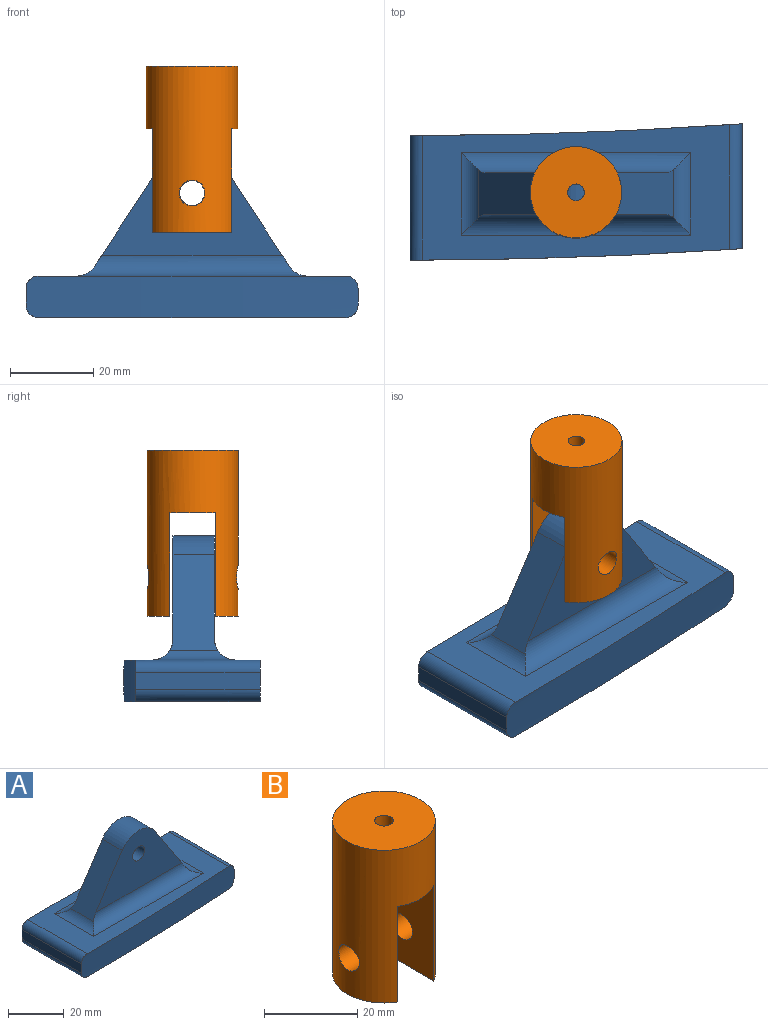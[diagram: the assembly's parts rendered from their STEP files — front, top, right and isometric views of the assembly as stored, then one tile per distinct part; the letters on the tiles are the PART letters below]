
ASSEMBLY  parts=2 mates=1
PART A: 20 faces, bbox 80x32.8x40 mm
  f0: plane 43.47x25mm, normal (0,1,0), area 641.4mm2, adj f8,f9,f10,f11,f12
  f1: plane 43.47x25mm, normal (0,-1,0), area 641.4mm2, adj f8,f9,f10,f11,f15
  f2: plane 74x32.63mm, normal (0,0,1), area 1113.5mm2, adj f4,f6,f12,f13,f14,f15,f18,f19
  f3: plane 30x4mm, normal (-1,0,0), area 120mm2, adj f4,f6,f17,f19
  f4: cylinder r=1158mm len=80mm, axis (0,0,-1), area 792.9mm2, adj f2,f3,f5,f7,f16,f17,f18,f19
  f5: plane 30.07x4mm, normal (1,0,0), area 120.3mm2, adj f4,f6,f16,f18
  f6: cylinder r=1128mm len=80mm, axis (0,0,-1), area 792.9mm2, adj f2,f3,f5,f7,f16,f17,f18,f19
  f7: plane 74x32.63mm, normal (0,0,-1), area 2221.8mm2, adj f4,f6,f16,f17
  f8: cylinder r=3mm len=10mm, axis (0,-1,0), area 188.5mm2, adj f0,f1
  f9: cylinder r=10mm len=16.75mm, axis (0,-1,0), area 198.5mm2, adj f0,f1,f10,f11
  f10: plane 23.2x15.15mm, normal (0.84,0,0.55), area 278.8mm2, adj f0,f1,f9,f12,f14,f15
  f11: plane 23.2x15.15mm, normal (-0.84,0,0.55), area 278.8mm2, adj f0,f1,f9,f12,f13,f15
  f12: cylinder r=5mm len=55.41mm, axis (-1,0,0), area 383.3mm2, adj f0,f2,f10,f11,f13,f14
  f13: cylinder r=5mm len=20mm, axis (0,-1,0), area 76.6mm2, adj f2,f11,f12,f15
  f14: cylinder r=5mm len=20mm, axis (0,-1,0), area 76.6mm2, adj f2,f10,f12,f15
  f15: cylinder r=5mm len=55.41mm, axis (1,0,0), area 383.3mm2, adj f1,f2,f10,f11,f13,f14
  f16: cylinder r=3mm len=30.28mm, axis (0,1,0), area 141.7mm2, adj f4,f5,f6,f7
  f17: cylinder r=3mm len=30mm, axis (0,-1,0), area 141.4mm2, adj f3,f4,f6,f7
  f18: cylinder r=3mm len=30.28mm, axis (0,-1,0), area 141.7mm2, adj f2,f4,f5,f6
  f19: cylinder r=3mm len=30mm, axis (0,1,0), area 141.4mm2, adj f2,f3,f4,f6
PART B: 11 faces, bbox 22x22x40 mm
  f0: plane 19.05x5.5mm, normal (0,0,-1), area 74.3mm2, adj f1,f5
  f1: cylinder r=11mm len=40mm, axis (0,0,-1), area 2127.7mm2, adj f0,f2,f3,f4,f5,f6,f7,f8
  f2: plane 22x22mm, normal (0,0,1), area 367.6mm2, adj f1,f9
  f3: plane 19.05x5.5mm, normal (0,0,-1), area 74.3mm2, adj f1,f6
  f4: plane 22x11mm, normal (0,0,-1), area 153mm2, adj f1,f5,f6,f10
  f5: plane 25x19.05mm, normal (-1,0,0), area 446.1mm2, adj f0,f1,f4,f8
  f6: plane 25x19.05mm, normal (1,0,0), area 446.1mm2, adj f1,f3,f4,f7
  f7: cylinder r=3.1mm len=6.2mm, axis (1,0,0), area 102.8mm2, adj f1,f6
  f8: cylinder r=3.1mm len=6.2mm, axis (1,0,0), area 102.8mm2, adj f1,f5
  f9: cylinder r=2mm len=12mm, axis (0,0,-1), area 150.8mm2, adj f2,f10
  f10: cone r=2mm half-angle=45deg, axis (0,0,-1), area 93.3mm2, adj f4,f9
PLACE A t=(-5,-0.25,-5.5)mm
PLACE B rot(axis=(0,0,1),90deg) t=(35,-14,15)mm
MATE revolute B.f7 <-> A.f8  axis (0,1,0) through (35,-19.5,24.5)mm
